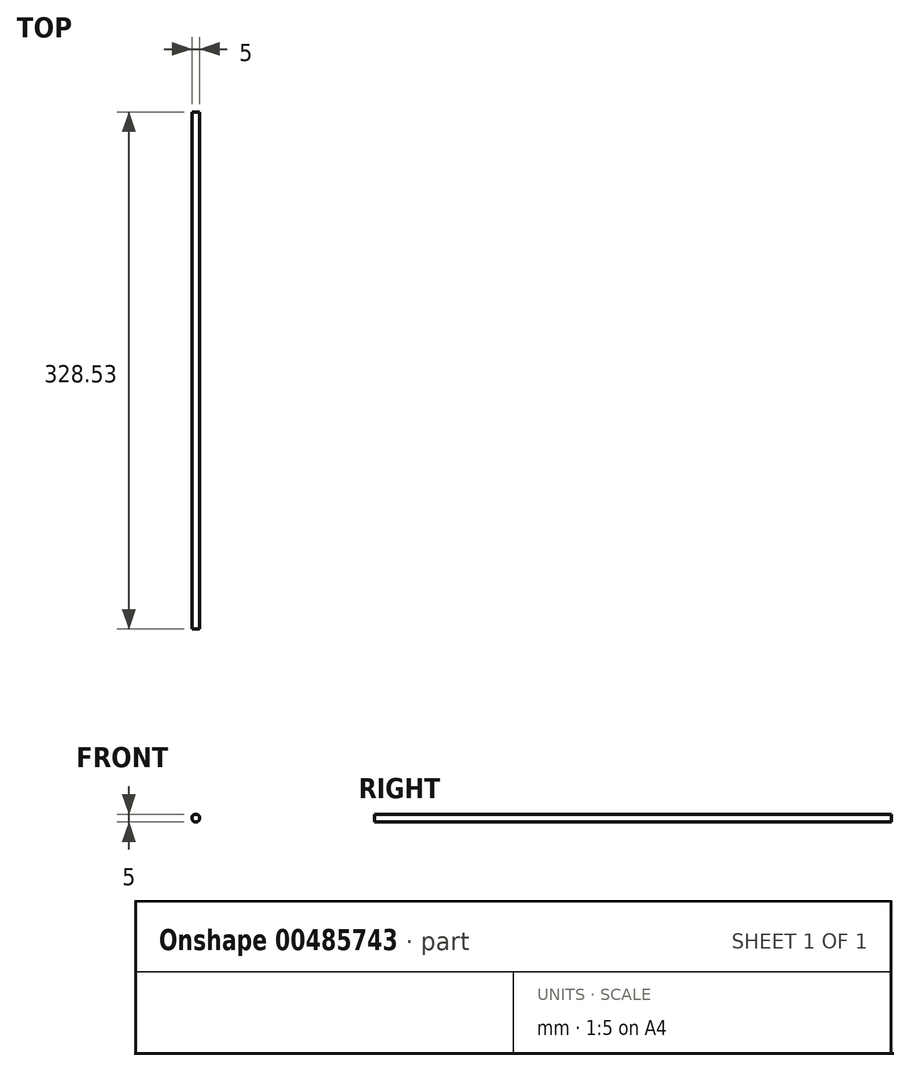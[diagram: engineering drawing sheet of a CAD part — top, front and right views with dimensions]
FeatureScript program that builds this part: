
annotation { "Feature Type Name" : "Feature", "Feature Type Description" : "" }
export const myFeature = defineFeature(function(context is Context, id is Id, definition is map)
    precondition{}
    {
        {
            var Q0;
            Q0=qCreatedBy(makeId("Front.planeOp"),FACE);
            var sketch = newSketch(context, id + "F0", { "sketchPlane" : qUnion([Q0])});
            skCircle(sketch, "E0", {"center": v(0, 0) * mm, "radius": 2.5 * mm});
            skSolve(sketch);
        }
        {
            var Q0;
            Q0 = qSketchRegion(id + "F0", true);
            extrude(context, id + "F1", {"entities" : qUnion([Q0]), "flatOperationType" : FlatOperationType.REMOVE, "thickness1" : 5 * mm, "thickness2" : 0 * mm, "thickness" : 5 * mm, "depth" : (311.13 + 2 * 6 + 2 * 2.7) * mm, "offsetDistance" : 25 * mm, "startOffsetBound" : StartOffsetType.BLIND, "startOffsetDistance" : 25 * mm, "domain" : OperationDomain.MODEL});
        }
    });
